# Revit family: Mondo
name_source: partatom
category: Mechanical Equipment
units: mm (PartAtom-declared; Revit-internal decimal feet)

## family parameters
Always vertical = Yes
Classification = None
Cut with Voids When Loaded = No
Part Type = Normal
Room Calculation Point = No
Round Connector Dimension = Use Diameter
Shared = No
Work Plane-Based = No

## types (4) — shared parameters
Diepte = 80 mm  [stored 0.262467 ft]
H openingen = 488 mm  [stored 1.60105 ft]
H openingen o = 478 mm  [stored 1.56824 ft]
Hoogte = 500 mm  [stored 1.64042 ft]
Kleur = Lacquer White
Licht grijs = Licht grijs
Manufacturer = Masterwatt B.V.
Phase = 1
Scherm = Screen
URL = https://masterwatt.nl
Voltage = 230 V
Zwart = Zwart
zero-valued in all types: Default Elevation

## per-type parameters (varying)
| type | Aantal openingen boven | Aantal openingen onder | Art. No. | Beugel breed | Beugel smal | Breedte | Model | Power (default) |
| Mondo_0750W | 35 | 24 | 429 756 411 | No | Yes | 750 mm  [stored 2.46063 ft] | Mondo 750W | 750 VA |
| Mondo_1500W | 50 | 39 | 429 756 414 | Yes | No | 1050 mm | Mondo 1500W | 1500 VA |
| Mondo_1000W | 35 | 24 | 429 756 412 | No | Yes | 750 mm  [stored 2.46063 ft] | Mondo 1000W | 1000 VA |
| Mondo_2000W | 50 | 39 | 429 756 416 | Yes | No | 1050 mm | Mondo 2000W | 2000 VA |

note: [stored X ft] marks values corroborated as IEEE doubles in the binary element streams (Revit-internal decimal feet)

## geometry (parser evidence)
native form markers: Sweep x37
no freeform markers — native parametric forms only
